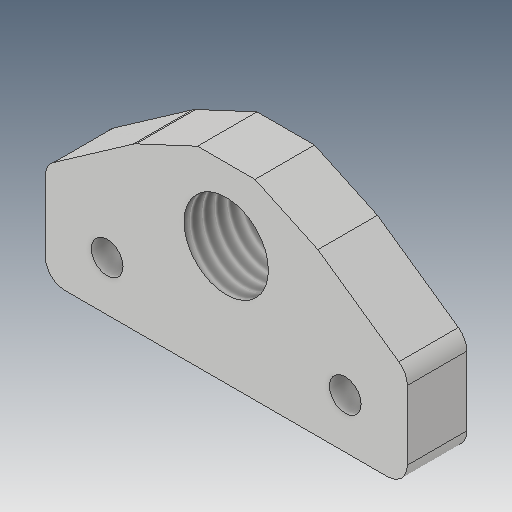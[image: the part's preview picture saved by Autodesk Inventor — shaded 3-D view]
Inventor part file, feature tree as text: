
AUTODESK INVENTOR PART (.ipt)
format: ipt  version: 2017 (Build 210142000, 142)  size: 124,928 bytes
history: native  units: mm
features: extrude x1, thread x1, sketch x1
ambient origin geometry x8: Origin, YZ Plane, XZ Plane, XY Plane, X Axis, Y Axis, Z Axis, Center Point
bodies: Solid1 (feature_tree)
feature tree (3):
  extrude  "Extrusion1"  Depth=10.0mm TaperAngle=0.0deg
  thread  "Thread1"  [1 undecoded]
  sketch  "Sketch1"  dims[d0=6.0mm d1=0.0mm d2=10.0mm d3=0.0mm]
note: 1 required parameter value undecoded (feature->parameter linkage not recoverable at this tier; creation-order binding heuristic only, values carry confidence <= 0.55)
